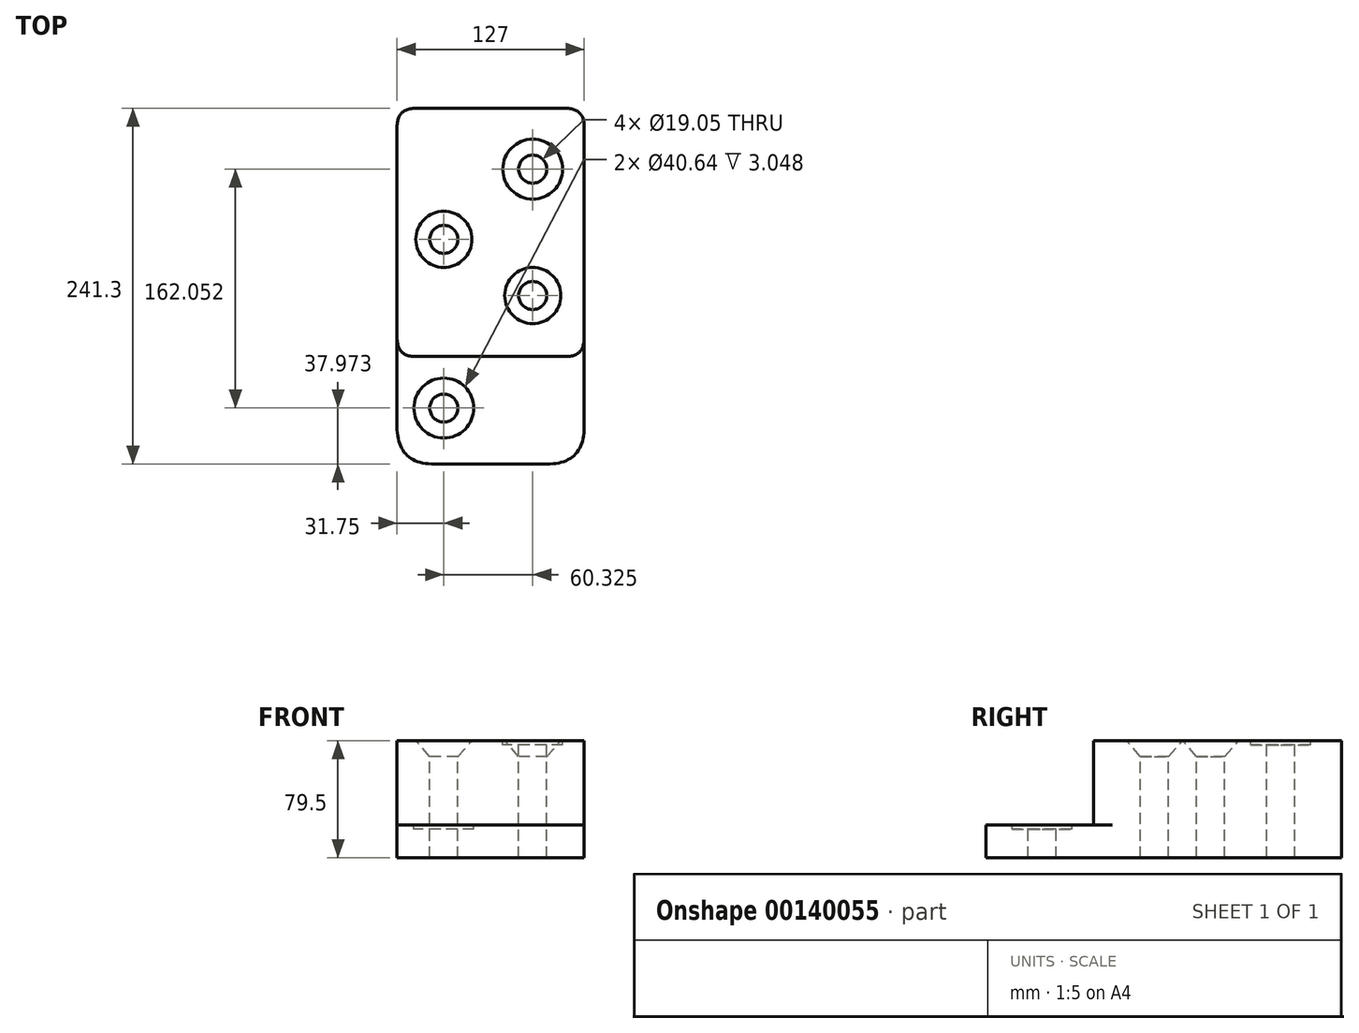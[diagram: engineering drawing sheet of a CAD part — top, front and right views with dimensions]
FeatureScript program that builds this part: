
annotation { "Feature Type Name" : "Feature", "Feature Type Description" : "" }
export const myFeature = defineFeature(function(context is Context, id is Id, definition is map)
    precondition{}
    {
        {
            var Q0;
            Q0=qCreatedBy(makeId("Front.planeOp"),FACE);
            var sketch = newSketch(context, id + "F0", { "sketchPlane" : qUnion([Q0])});
            skLineSegment(sketch, "E0.bottom", {"start": v(0, 0) * mm, "end": v(127, 0) * mm});
            skLineSegment(sketch, "E0.top", {"start": v(0, 22.35) * mm, "end": v(127, 22.35) * mm});
            skLineSegment(sketch, "E0.left", {"start": v(0, 0) * mm, "end": v(0, 22.35) * mm});
            skLineSegment(sketch, "E0.right", {"start": v(127, 0) * mm, "end": v(127, 22.35) * mm});
            skSolve(sketch);
        }
        {
            var Q0;
            Q0 = qSketchRegion(id + "F0", true);
            extrude(context, id + "F1", {"entities" : qUnion([Q0]), "oppositeDirection" : true, "depth" : 241.3 * mm});
        }
        {
            var Q0;
            Q0=makeQuery(id+"F1.opExtrude","SWEPT_FACE",FACE,{"disambiguationData":[OSD([sQuery(id+"F0.wireOp",EDGE,"E0.top")])]});
            var sketch = newSketch(context, id + "F2", { "sketchPlane" : qUnion([Q0])});
            skLineSegment(sketch, "E1.bottom", {"start": v(0, 241.3) * mm, "end": v(127, 241.3) * mm});
            skLineSegment(sketch, "E1.top", {"start": v(0, 72.9) * mm, "end": v(127, 72.9) * mm});
            skLineSegment(sketch, "E1.left", {"start": v(0, 241.3) * mm, "end": v(0, 72.9) * mm});
            skLineSegment(sketch, "E1.right", {"start": v(127, 241.3) * mm, "end": v(127, 72.9) * mm});
            skSolve(sketch);
        }
        {
            var Q0;
            Q0 = qSketchRegion(id + "F2", true);
            extrude(context, id + "F3", {"entities" : qUnion([Q0]), "operationType" : NewBodyOperationType.ADD, "depth" : 57.15 * mm});
        }
        {
            var Q0;
            Q0=makeQuery(id+"F3.opExtrude","CAP_FACE",FACE,{"disambiguationData":[OSD([sQuery(id+"F2.wireOp",EDGE,"E1.bottom"),sQuery(id+"F2.wireOp",EDGE,"E1.top"),sQuery(id+"F2.wireOp",EDGE,"E1.left"),sQuery(id+"F2.wireOp",EDGE,"E1.right")])],"isStart":false});
            var sketch = newSketch(context, id + "F4", { "sketchPlane" : qUnion([Q0])});
            skPoint(sketch, "E2", {"position": v(92.07, 200.03) * mm});
            skPoint(sketch, "E3", {"position": v(92.07, 114.3) * mm});
            skPoint(sketch, "E4", {"position": v(31.75, 152.4) * mm});
            skPoint(sketch, "E5", {"position": v(31.75, 37.97) * mm});
            skSolve(sketch);
        }
        {
            var Q0;
            Q0=sQuery(id+"F4.wireOp",VERTEX,"E4");
            var Q1;
            Q1=sQuery(id+"F4.wireOp",VERTEX,"E3");
            var Q2;
            Q2=makeQuery(id+"F1.opExtrude","SWEPT_BODY",BODY,{"disambiguationData":[OSD([sQuery(id+"F0.wireOp",EDGE,"E0.bottom"),sQuery(id+"F0.wireOp",EDGE,"E0.top"),sQuery(id+"F0.wireOp",EDGE,"E0.left"),sQuery(id+"F0.wireOp",EDGE,"E0.right")])]});
            hole(context, id + "F5", {"style" : HoleStyle.C_SINK, "endStyle" : HoleEndStyle.THROUGH, "holeDiameter" : 19.05 * mm, "cSinkDiameter" : 38.1 * mm, "cSinkAngle" : 82 * degree, "locations" : qUnion([Q0, Q1]), "scope" : qUnion([Q2]), "isTappedThrough" : true});
        }
        {
            var Q0;
            Q0=sQuery(id+"F4.wireOp",VERTEX,"E2");
            var Q1;
            Q1=sQuery(id+"F4.wireOp",VERTEX,"E5");
            var Q2;
            Q2=makeQuery(id+"F1.opExtrude","SWEPT_BODY",BODY,{"disambiguationData":[OSD([sQuery(id+"F0.wireOp",EDGE,"E0.bottom"),sQuery(id+"F0.wireOp",EDGE,"E0.top"),sQuery(id+"F0.wireOp",EDGE,"E0.left"),sQuery(id+"F0.wireOp",EDGE,"E0.right")])]});
            hole(context, id + "F6", {"style" : HoleStyle.C_BORE, "endStyle" : HoleEndStyle.THROUGH, "holeDiameter" : 19.05 * mm, "cBoreDiameter" : 40.64 * mm, "cBoreDepth" : 3.05 * mm, "locations" : qUnion([Q0, Q1]), "scope" : qUnion([Q2]), "isTappedThrough" : true});
        }
        {
            var Q0;
            Q0=makeQuery(id+"F1.opExtrude","CAP_EDGE",EDGE,{"disambiguationData":[OSD([sQuery(id+"F0.wireOp",EDGE,"E0.right")])],"isStart":true});
            fillet(context, id + "F7", {"entities" : qUnion([Q0]), "radius" : 25.4 * mm, "rho" : .5, "crossSection" : FilletCrossSection.CONIC, "allowEdgeOverflow" : false});
        }
        {
            var Q0;
            Q0=makeQuery(id+"F3.opExtrude","SWEPT_EDGE",EDGE,{"disambiguationData":[OSD([sQuery(id+"F0.wireOp",EDGE,"E0.top"),sQuery(id+"F0.wireOp",EDGE,"E0.right"),sQuery(id+"F2.wireOp",EDGE,"E1.top"),sQuery(id+"F2.wireOp",EDGE,"E1.right")])]});
            fillet(context, id + "F8", {"entities" : qUnion([Q0]), "radius" : 12.7 * mm, "tangentPropagation" : true, "rho" : .5, "crossSection" : FilletCrossSection.CONIC, "allowEdgeOverflow" : false});
        }
        {
            var Q0;
            Q0=makeQuery(id+"F3.opExtrude","SWEPT_EDGE",EDGE,{"disambiguationData":[OSD([sQuery(id+"F0.wireOp",EDGE,"E0.top"),sQuery(id+"F0.wireOp",EDGE,"E0.left"),sQuery(id+"F2.wireOp",EDGE,"E1.top"),sQuery(id+"F2.wireOp",EDGE,"E1.left")])]});
            fillet(context, id + "F9", {"entities" : qUnion([Q0]), "radius" : 12.7 * mm, "tangentPropagation" : true, "rho" : 0.5, "crossSection" : FilletCrossSection.CONIC, "allowEdgeOverflow" : false});
        }
        {
            var Q0;
            Q0=makeQuery(id+"F1.opExtrude","CAP_EDGE",EDGE,{"disambiguationData":[OSD([sQuery(id+"F0.wireOp",EDGE,"E0.left")])],"isStart":true});
            fillet(context, id + "F10", {"entities" : qUnion([Q0]), "radius" : 25.4 * mm, "tangentPropagation" : true, "rho" : 0.5, "crossSection" : FilletCrossSection.CONIC, "allowEdgeOverflow" : false});
        }
        {
            var Q0;
            Q0=makeQuery(id+"F3.boolean.opBoolean","MERGE",EDGE,{"derivedFrom":[makeQuery(id+"F1.opExtrude","CAP_EDGE",EDGE,{"disambiguationData":[OSD([sQuery(id+"F0.wireOp",EDGE,"E0.right")])],"isStart":false}),makeQuery(id+"F3.opExtrude","SWEPT_EDGE",EDGE,{"disambiguationData":[OSD([sQuery(id+"F2.wireOp",EDGE,"E1.bottom"),sQuery(id+"F2.wireOp",EDGE,"E1.right")])]})]});
            fillet(context, id + "F11", {"entities" : qUnion([Q0]), "radius" : 12.7 * mm, "tangentPropagation" : true, "rho" : 0.5, "crossSection" : FilletCrossSection.CONIC, "allowEdgeOverflow" : false});
        }
        {
            var Q0;
            Q0=makeQuery(id+"F3.boolean.opBoolean","MERGE",EDGE,{"derivedFrom":[makeQuery(id+"F1.opExtrude","CAP_EDGE",EDGE,{"disambiguationData":[OSD([sQuery(id+"F0.wireOp",EDGE,"E0.left")])],"isStart":false}),makeQuery(id+"F3.opExtrude","SWEPT_EDGE",EDGE,{"disambiguationData":[OSD([sQuery(id+"F2.wireOp",EDGE,"E1.bottom"),sQuery(id+"F2.wireOp",EDGE,"E1.left")])]})]});
            fillet(context, id + "F12", {"entities" : qUnion([Q0]), "radius" : 12.7 * mm, "tangentPropagation" : true, "rho" : 0.5, "crossSection" : FilletCrossSection.CONIC, "allowEdgeOverflow" : false});
        }
    });
